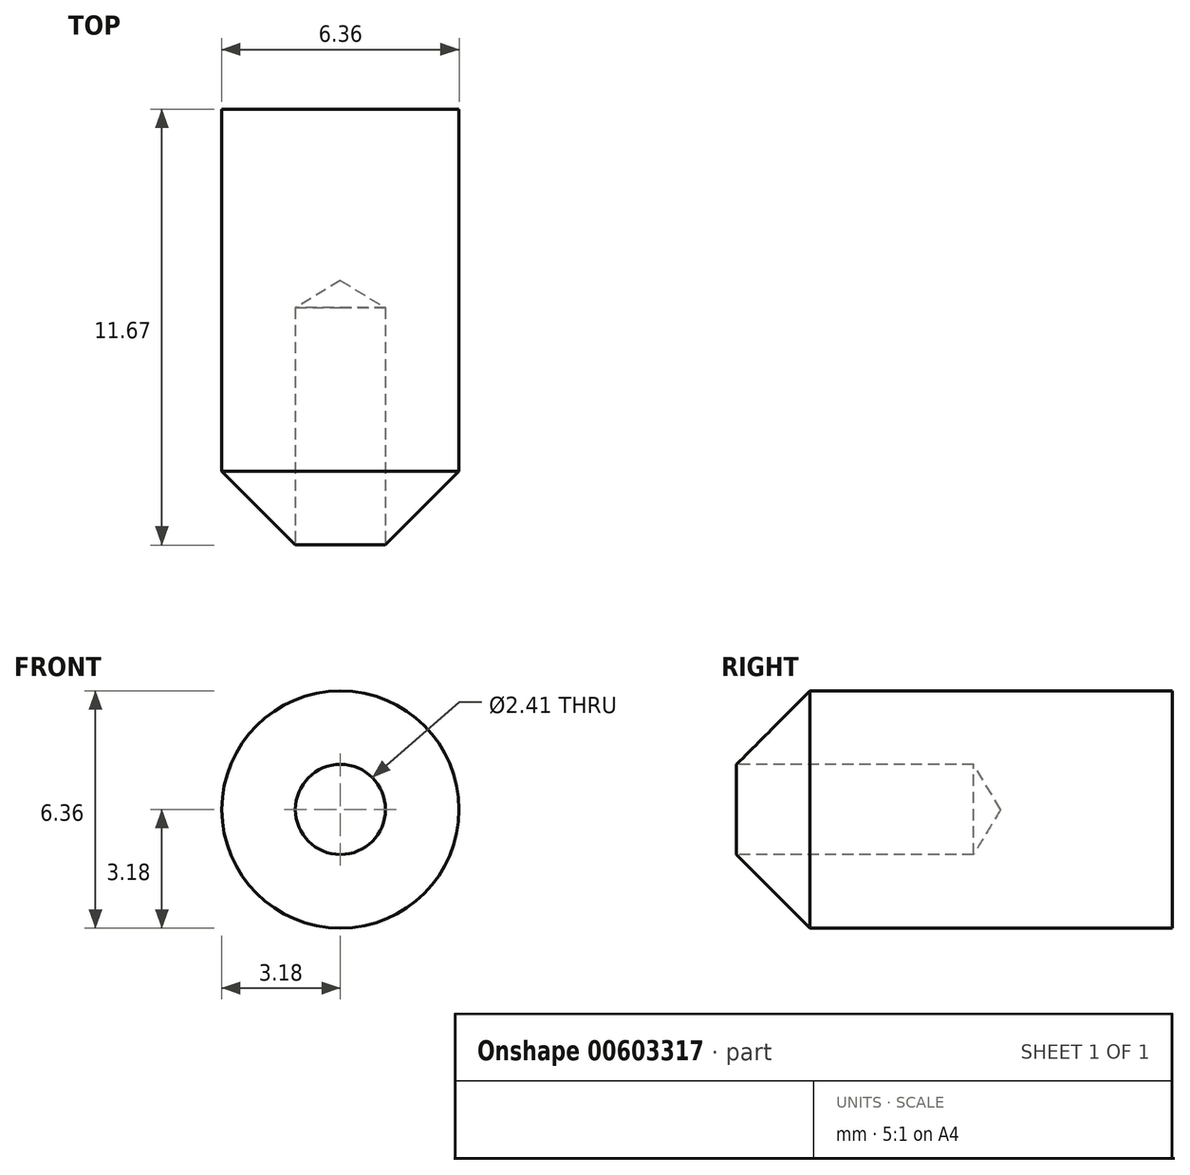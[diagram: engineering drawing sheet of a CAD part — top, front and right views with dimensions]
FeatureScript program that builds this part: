
annotation { "Feature Type Name" : "Feature", "Feature Type Description" : "" }
export const myFeature = defineFeature(function(context is Context, id is Id, definition is map)
    precondition{}
    {
        {
            var Q0;
            Q0=qCreatedBy(makeId("Front.planeOp"),FACE);
            var sketch = newSketch(context, id + "F0", { "sketchPlane" : qUnion([Q0])});
            skCircle(sketch, "E0", {"center": v(0, 0) * mm, "radius": 3.18 * mm});
            skSolve(sketch);
        }
        {
            var Q0;
            Q0 = qSketchRegion(id + "F0", true);
            extrude(context, id + "F1", {"entities" : qUnion([Q0]), "depth" : 12.7 * mm, "offsetDistance" : 25 * mm});
        }
        {
            var Q0;
            Q0=makeQuery(id+"F1.opExtrude","CAP_EDGE",EDGE,{"disambiguationData":[OSD([sQuery(id+"F0.wireOp",EDGE,"E0")])],"isStart":false});
            chamfer(context, id + "F2", {"entities" : qUnion([Q0]), "width" : 3 * mm, "tangentPropagation" : true});
        }
        {
            var Q0;
            Q0=makeQuery(id+"F1.opExtrude","CAP_FACE",FACE,{"disambiguationData":[OSD([sQuery(id+"F0.wireOp",EDGE,"E0")])],"isStart":false});
            var sketch = newSketch(context, id + "F3", { "sketchPlane" : qUnion([Q0])});
            skCircle(sketch, "E1", {"center": v(0, 0) * mm, "radius": 1.25 * mm});
            skSolve(sketch);
        }
        {
            var Q0;
            Q0=sQuery(id+"F3.wireOp",VERTEX,"E1.center");
            var Q1;
            Q1=makeQuery(id+"F1.opExtrude","SWEPT_BODY",BODY,{"disambiguationData":[OSD([sQuery(id+"F0.wireOp",EDGE,"E0")])]});
            hole(context, id + "F4", {"style" : HoleStyle.SIMPLE, "endStyle" : HoleEndStyle.BLIND, "holeDiameter" : 2.41 * mm, "majorDiameter" : 5 * mm, "holeDepth" : 6.35 * mm, "isTappedThrough" : true, "tappedDepth" : 12 * mm, "tapClearance" : 3, "locations" : qUnion([Q0]), "scope" : qUnion([Q1])});
        }
    });
